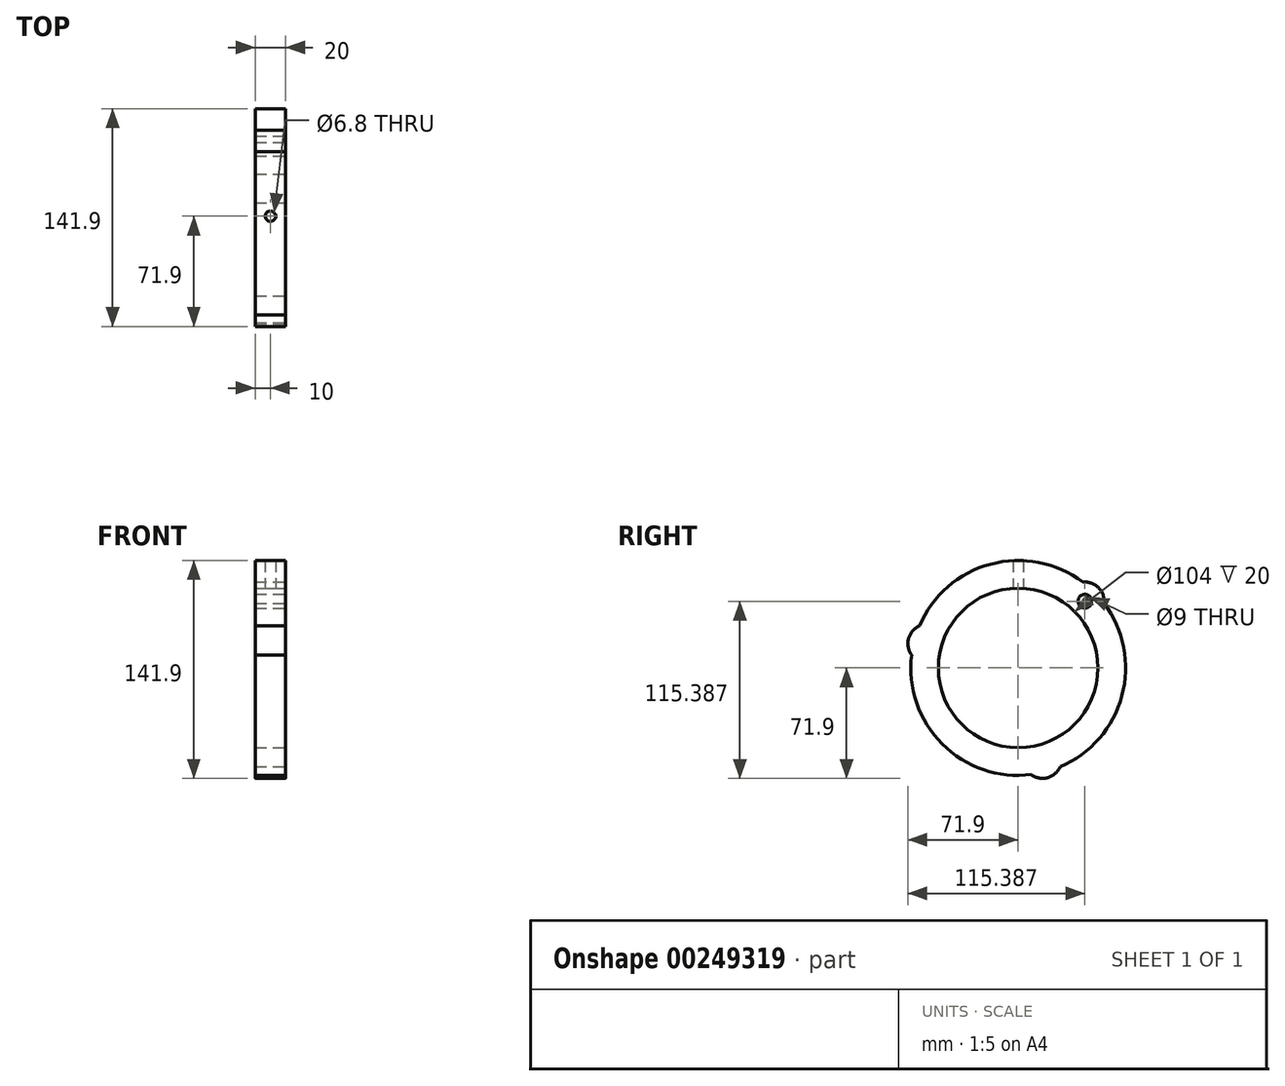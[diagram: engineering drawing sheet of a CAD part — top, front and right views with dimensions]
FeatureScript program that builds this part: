
annotation { "Feature Type Name" : "Feature", "Feature Type Description" : "" }
export const myFeature = defineFeature(function(context is Context, id is Id, definition is map)
    precondition{}
    {
        {
            var Q0;
            Q0=qCreatedBy(makeId("Front.planeOp"),FACE);
            var sketch = newSketch(context, id + "F0", { "sketchPlane" : qUnion([Q0])});
            skLineSegment(sketch, "E0", {"start": v(0, 0) * mm, "end": v(-96.69, 0) * mm});
            skLineSegment(sketch, "E1", {"start": v(0, 52) * mm, "end": v(-20, 52) * mm});
            skLineSegment(sketch, "E2", {"start": v(-20, 52) * mm, "end": v(-20, 70) * mm});
            skLineSegment(sketch, "E3", {"start": v(-20, 70) * mm, "end": v(0, 70) * mm});
            skLineSegment(sketch, "E4", {"start": v(0, 70) * mm, "end": v(0, 52) * mm});
            skSolve(sketch);
        }
        {
            var Q0;
            Q0=makeQuery(id+"F0.imprint","IMPRINT",FACE,{"disambiguationData":[TD([[makeQuery(id+"F0.imprint","IMPRINT",EDGE,{"derivedFrom":sQuery(id+"F0.wireOp",EDGE,"E1")}),-1.0]])]});
            var Q1;
            Q1=sQuery(id+"F0.wireOp",EDGE,"E0");
            revolve(context, id + "F1", {"entities" : qUnion([Q0]), "axis" : qUnion([Q1]), "revolveType" : RevolveType.FULL});
        }
        {
            var Q0;
            Q0=qCreatedBy(makeId("Top.planeOp"),FACE);
            var sketch = newSketch(context, id + "F2", { "sketchPlane" : qUnion([Q0])});
            skCircle(sketch, "E5", {"center": v(-10, 0) * mm, "radius": 3.4 * mm});
            skSolve(sketch);
        }
        {
            var Q0;
            Q0=makeQuery(id+"F2.imprint","IMPRINT",FACE,{"disambiguationData":[TD([[makeQuery(id+"F2.imprint","IMPRINT",EDGE,{"derivedFrom":sQuery(id+"F2.wireOp",EDGE,"E5")}),1.0]])]});
            extrude(context, id + "F3", {"entities" : qUnion([Q0]), "operationType" : NewBodyOperationType.REMOVE, "depth" : 100 * mm});
        }
        {
            var Q0;
            Q0=qCreatedBy(makeId("Right.planeOp"),FACE);
            var sketch = newSketch(context, id + "F4", { "sketchPlane" : qUnion([Q0])});
            skLineSegment(sketch, "E6", {"start": v(0, 0) * mm, "end": v(43.49, 43.49) * mm, "construction": true});
            skCircle(sketch, "E7", {"center": v(0, 0) * mm, "radius": 61.5 * mm, "construction": true});
            skCircle(sketch, "E8", {"center": v(43.49, 43.49) * mm, "radius": 4.5 * mm});
            skSolve(sketch);
        }
        {
            var Q0;
            Q0=makeQuery(id+"F4.imprint","IMPRINT",FACE,{"disambiguationData":[TD([[makeQuery(id+"F4.imprint","IMPRINT",EDGE,{"derivedFrom":sQuery(id+"F4.wireOp",EDGE,"E8")}),1.0]])]});
            extrude(context, id + "F5", {"entities" : qUnion([Q0]), "operationType" : NewBodyOperationType.REMOVE, "oppositeDirection" : true, "depth" : 40 * mm, "symmetric" : true});
        }
        {
            var Q0;
            Q0=qCreatedBy(makeId("Right.planeOp"),FACE);
            var sketch = newSketch(context, id + "F6", { "sketchPlane" : qUnion([Q0])});
            skCircle(sketch, "E9.0", {"center": v(43.49, 43.49) * mm, "radius": 4.5 * mm, "construction": true});
            skCircle(sketch, "E10.0", {"center": v(-59.4, 15.92) * mm, "radius": 4.5 * mm, "construction": true});
            skCircle(sketch, "E11.0", {"center": v(15.92, -59.4) * mm, "radius": 4.5 * mm, "construction": true});
            skArc(sketch, "E12.0", {"start": v(55.91, 42.12) * mm, "mid": v(49.5, 49.5) * mm, "end": v(42.12, 55.91) * mm});
            skArc(sketch, "E13", {"start": v(55.91, 42.12) * mm, "mid": v(52.33, 52.33) * mm, "end": v(42.12, 55.91) * mm});
            skArc(sketch, "E14", {"start": v(-64.43, 27.36) * mm, "mid": v(-71.48, 19.15) * mm, "end": v(-69.48, 8.52) * mm});
            skArc(sketch, "E15", {"start": v(8.52, -69.48) * mm, "mid": v(19.15, -71.48) * mm, "end": v(27.36, -64.43) * mm});
            skArc(sketch, "E16.trimOffspring", {"start": v(8.52, -69.48) * mm, "mid": v(18.12, -67.61) * mm, "end": v(27.36, -64.43) * mm});
            skArc(sketch, "E17.trimOffspring", {"start": v(-64.43, 27.36) * mm, "mid": v(-67.61, 18.12) * mm, "end": v(-69.48, 8.52) * mm});
            skSolve(sketch);
        }
        {
            var Q0;
            Q0=makeQuery(id+"F6.imprint","IMPRINT",FACE,{"disambiguationData":[TD([[makeQuery(id+"F6.imprint","IMPRINT",EDGE,{"derivedFrom":sQuery(id+"F6.wireOp",EDGE,"E14")}),1.0]])]});
            var Q1;
            Q1=makeQuery(id+"F6.imprint","IMPRINT",FACE,{"disambiguationData":[TD([[makeQuery(id+"F6.imprint","IMPRINT",EDGE,{"derivedFrom":sQuery(id+"F6.wireOp",EDGE,"E15")}),1.0]])]});
            var Q2;
            Q2=makeQuery(id+"F6.imprint","IMPRINT",FACE,{"disambiguationData":[TD([[makeQuery(id+"F6.imprint","IMPRINT",EDGE,{"derivedFrom":sQuery(id+"F6.wireOp",EDGE,"E12.0")}),-1.0]])]});
            extrude(context, id + "F7", {"entities" : qUnion([Q0, Q1, Q2]), "operationType" : NewBodyOperationType.ADD, "oppositeDirection" : true, "depth" : 20 * mm});
        }
    });
